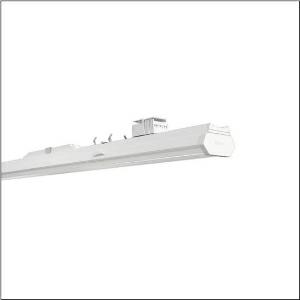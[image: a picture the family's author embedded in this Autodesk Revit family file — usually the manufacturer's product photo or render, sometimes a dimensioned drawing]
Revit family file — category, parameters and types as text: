
# Revit family: licross_r__21_protected_mo_52tp12dn4a5g_b875
name_source: partatom
category: Lighting Fixtures
units: mm (PartAtom-declared; Revit-internal decimal feet)

## family parameters
Cut with Voids When Loaded = No
Host = Face
Light Source = No
Part Type = Normal
Room Calculation Point = No
Round Connector Dimension = Use Diameter
Shared = No

## types (1)
- --- (1 x LED, 10700 lm, 62 W, 4000K)
    Apparent Load = 62 VA
    CIE Flux Codes = 73 92 98 99 100
    Color Rendering = 80
    Color Temperature = 4000K
    Default Elevation = 1800 mm
    Description = Licross® 21 Protected MO, luminaire insert, of sheet steel, galvanised, coil coated, white, length: 1.500mm, width: 90mm, height: 103mm, LED rated luminous flux: 10.700lm, light colour: 840, control gear: DALI 2, with plug, 5-pole, with phase selection, mains connection: 220..240V, AC, 50/60Hz, rated input power: 62W, internal wiring halogen-free, primary light control with lens, of plastic, primary optical cover: cover, of PMMA, light emission: direct distribution, primary light characteristic: symmetric, protection rating (complete): IP64, insulation class (complete): insulation class I (protective earthing), certification: CE, ENEC, VDE, UKCA, protection symbol: D if used in an environment with conductive dust loads with corresponding accessories, impact resistance: IK06, permissible ambient temperature for indoor applications: -25..+35°C, corresponds to IFS (International Featured Standards) requirements for safety and quality in the food industry, reducing of maximum allowable ambient temperature of 5°C with ceiling mounting, LABS conformity tested according to VDMA 24364:2018-05, packaging unit: 1 piece
    Height = 92 mm
    Lamp = 1 x LED
    Lamp Light Flux = 10700 lm
    Lamp Power = 62 W
    Lamp count = 1
    Length = 1500 mm
    Luminous efficacy = 173 lm/W
    Manufacturer = Siteco
    ModVariant = No
    Model = 52TP12DN4A5G
    Mounting Place = Ceiling
    Mounting Type = Pendant
    Number of Poles = 1
    OnlyDefault = Yes
    Power Factor = 1
    Product Name = Licross® 21 Protected MO
    Product group = luminaire insert | ceiling pendant
    ProductGroupID = 902
    Protection Class = Protection class I
    Protection Degree = IP 64
    RLX_Detail_Level = 1
    RLX_Emergency_Light_Flux = 0 lm
    RLX_Emergency_Type = 0
    RLX_Emergency_Type_DB = No
    RlxData = <blob elided: 24529 chars, md5=beb8080e>
    Socket = socket
    Standby Power = 0 W
    System Light Flux = 10700 lm
    System Power = 62 W
    Type Comments = factory setting: luminous flux: 100 % | dim-lin: 254 | 418 mA
    Type Image = l_1256148.jpg
    URL = http://relux.com
    VarID = @adj_150199
    Voltage = 0 V
    Weight = 0.00 kg
    Width = 88 mm

## geometry (parser evidence)
native form markers: Blend x4, Sweep x11
no freeform markers — native parametric forms only
